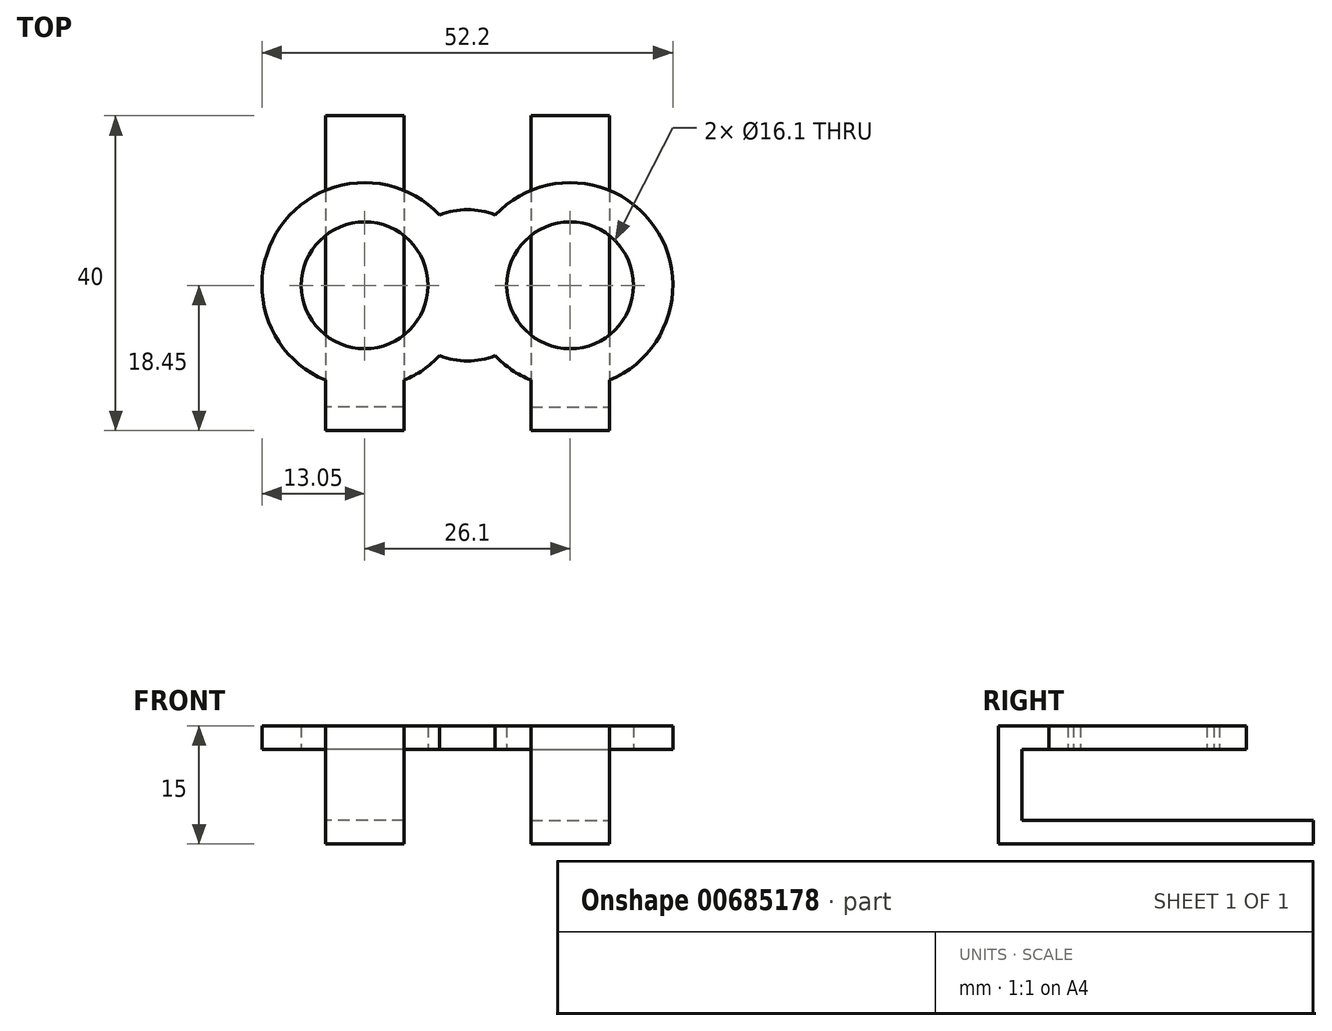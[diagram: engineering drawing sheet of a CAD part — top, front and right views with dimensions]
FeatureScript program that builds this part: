
annotation { "Feature Type Name" : "Feature", "Feature Type Description" : "" }
export const myFeature = defineFeature(function(context is Context, id is Id, definition is map)
    precondition{}
    {
        {
            var Q0;
            Q0=qCreatedBy(makeId("Top.planeOp"),FACE);
            var sketch = newSketch(context, id + "F0", { "sketchPlane" : qUnion([Q0])});
            skPoint(sketch, "E0.middle", {"position": v(0, 0) * mm});
            skCircle(sketch, "E1", {"center": v(-13.05, 0) * mm, "radius": 8.05 * mm});
            skCircle(sketch, "E2.0", {"center": v(-13.05, 0) * mm, "radius": 13.05 * mm});
            skArc(sketch, "E3", {"start": v(0, 9.6) * mm, "mid": v(-1.8, 9.44) * mm, "end": v(-3.54, 8.93) * mm});
            skArc(sketch, "E4", {"start": v(-3.54, -8.93) * mm, "mid": v(-1.8, -9.44) * mm, "end": v(0, -9.6) * mm});
            skLineSegment(sketch, "E5", {"start": v(0, 9.6) * mm, "end": v(0, -9.6) * mm});
            skSolve(sketch);
        }
        {
            var Q0;
            Q0 = qSketchRegion(id + "F0", true);
            extrude(context, id + "F1", {"entities" : qUnion([Q0]), "depth" : 3 * mm, "offsetDistance" : 25 * mm});
        }
        {
            var Q0;
            Q0=makeQuery(id+"F1.opExtrude","CAP_FACE",FACE,{"disambiguationData":[OSD([sQuery(id+"F0.wireOp",EDGE,"u3PScjyl-kRYi-sbIx-EU0c-YE49KCThl473"),sQuery(id+"F0.wireOp",EDGE,"E1"),sQuery(id+"F0.wireOp",EDGE,"6eeaa10e-91e7-4207-8f49-f0e361722820.0"),sQuery(id+"F0.wireOp",EDGE,"E2.0")])],"isStart":true});
            var sketch = newSketch(context, id + "F2", { "sketchPlane" : qUnion([Q0])});
            skLineSegment(sketch, "E6.bottom", {"start": v(-8.05, 8.05) * mm, "end": v(-18.05, 8.05) * mm});
            skLineSegment(sketch, "E6.top", {"start": v(-8.05, 15.45) * mm, "end": v(-18.05, 15.45) * mm});
            skLineSegment(sketch, "E6.left", {"start": v(-8.05, 8.05) * mm, "end": v(-8.05, 15.45) * mm});
            skLineSegment(sketch, "E6.right", {"start": v(-18.05, 8.05) * mm, "end": v(-18.05, 15.45) * mm});
            skPoint(sketch, "E6.middle", {"position": v(-13.05, 11.75) * mm});
            skLineSegment(sketch, "E7", {"start": v(-21.1, 0) * mm, "end": v(-5, 0) * mm, "construction": true});
            skPoint(sketch, "E7.startSnap0", {"position": v(-26, 0) * mm});
            skPoint(sketch, "E8", {"position": v(-13.05, 0) * mm});
            skLineSegment(sketch, "E9", {"start": v(-13.05, 0) * mm, "end": v(-13.05, 14.02) * mm, "construction": true});
            skPoint(sketch, "E10", {"position": v(-13.05, 15.45) * mm});
            skLineSegment(sketch, "E11.0", {"start": v(-8.05, 18.45) * mm, "end": v(-18.05, 18.45) * mm});
            skLineSegment(sketch, "E12", {"start": v(-18.05, 15.45) * mm, "end": v(-18.05, 18.45) * mm});
            skLineSegment(sketch, "E13", {"start": v(-8.05, 18.45) * mm, "end": v(-8.05, 15.45) * mm});
            skSolve(sketch);
        }
        {
            var Q0;
            {var subQ5=sQuery(id+"F2.wireOp",EDGE,"E6.top");Q0=makeQuery(id+"F2.imprint","IMPRINT",FACE,{"disambiguationData":[TD([[makeQuery(id+"F2.imprint","IMPRINT",EDGE,{"derivedFrom":subQ5}),1.0]])]});}
            var Q1;
            Q1=makeQuery(id+"F2.imprint","IMPRINT",FACE,{"disambiguationData":[TD([[makeQuery(id+"F2.imprint","IMPRINT",EDGE,{"derivedFrom":sQuery(id+"F2.wireOp",EDGE,"E6.top")}),-1.0]])]});
            var Q2;
            Q2=makeQuery(id+"F1.opExtrude","CAP_FACE",FACE,{"disambiguationData":[OSD([sQuery(id+"F0.wireOp",EDGE,"E1"),sQuery(id+"F0.wireOp",EDGE,"E2.0")])],"isStart":false});
            extrude(context, id + "F3", {"entities" : qUnion([Q0, Q1]), "operationType" : NewBodyOperationType.ADD, "endBound" : BoundingType.UP_TO_SURFACE, "oppositeDirection" : true, "depth" : 3 * mm, "endBoundEntityFace" : qUnion([Q2]), "offsetDistance" : 25 * mm});
        }
        {
            var Q0;
            Q0=makeQuery(id+"F2.imprint","IMPRINT",FACE,{"disambiguationData":[TD([[makeQuery(id+"F2.imprint","IMPRINT",EDGE,{"derivedFrom":sQuery(id+"F2.wireOp",EDGE,"E6.top")}),-1.0]])]});
            extrude(context, id + "F4", {"entities" : qUnion([Q0]), "operationType" : NewBodyOperationType.ADD, "depth" : 9 * mm, "offsetDistance" : 25 * mm});
        }
        {
            var Q0;
            {var subQ0=sQuery(id+"F2.wireOp",EDGE,"E11.0");Q0=makeQuery(id+"F4.boolean.opBoolean","MERGE",FACE,{"derivedFrom":[makeQuery(id+"F3.opExtrude","SWEPT_FACE",FACE,{"disambiguationData":[OSD([subQ0])]}),makeQuery(id+"F4.opExtrude","SWEPT_FACE",FACE,{"disambiguationData":[OSD([subQ0])]})]});}
            var sketch = newSketch(context, id + "F5", { "sketchPlane" : qUnion([Q0])});
            skLineSegment(sketch, "E14.bottom", {"start": v(-18.05, -9) * mm, "end": v(-8.05, -9) * mm});
            skLineSegment(sketch, "E14.top", {"start": v(-18.05, -12) * mm, "end": v(-8.05, -12) * mm});
            skLineSegment(sketch, "E14.left", {"start": v(-18.05, -9) * mm, "end": v(-18.05, -12) * mm});
            skLineSegment(sketch, "E14.right", {"start": v(-8.05, -9) * mm, "end": v(-8.05, -12) * mm});
            skSolve(sketch);
        }
        {
            var Q0;
            Q0=makeQuery(id+"F5.imprint","IMPRINT",FACE,{"disambiguationData":[TD([[makeQuery(id+"F5.imprint","IMPRINT",EDGE,{"derivedFrom":sQuery(id+"F5.wireOp",EDGE,"E14.bottom")}),1.0]])]});
            extrude(context, id + "F6", {"entities" : qUnion([Q0]), "operationType" : NewBodyOperationType.ADD, "oppositeDirection" : true, "depth" : 40 * mm, "offsetDistance" : 25 * mm});
        }
        {
            var Q0;
            Q0=makeQuery(id+"F1.opExtrude","SWEPT_BODY",BODY,{"disambiguationData":[OSD([sQuery(id+"F0.wireOp",EDGE,"E1"),sQuery(id+"F0.wireOp",EDGE,"E2.0")])]});
            var Q1;
            Q1=qCreatedBy(makeId("Right.planeOp"),FACE);
            mirror(context, id + "F7", {"operationType" : NewBodyOperationType.ADD, "entities" : qUnion([Q0]), "mirrorPlane" : qUnion([Q1])});
        }
    });
